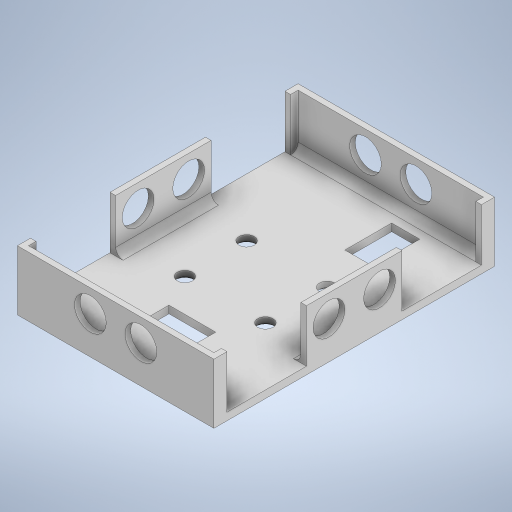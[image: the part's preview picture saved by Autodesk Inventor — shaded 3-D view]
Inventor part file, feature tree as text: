
AUTODESK INVENTOR PART (.ipt)
format: ipt  version: 2024.2 (Build 282272000, 272)  size: 484,352 bytes
history: native  units: mm
features: extrude x11, sketch x11, fillet x2, chamfer x1
ambient origin geometry x8: Origin, YZ Plane, XZ Plane, XY Plane, X Axis, Y Axis, Z Axis, Center Point
bodies: Solid1 (feature_tree)
feature tree (25):
  extrude  "Extrusion1"  Depth=48.0mm
  extrude  "Extrusion3"  Depth=4.7mm
  extrude  "Extrusion4"  Depth=4.7mm
  extrude  "remove legs"  Depth=43.0mm
  extrude  "Extrusion6"  Depth=7.5mm
  extrude  "Extrusion7"  Depth=7.5mm
  chamfer  "Chamfer1"  Distance=10.0mm
  sketch  "Sketch7"  dims[d12=7.500001mm]
  sketch  "Sketch8"  dims[d13=7.500001mm]
  sketch  "Sketch9"  dims[d14=10.0mm]
  extrude  "Extrusion10"  Depth=13.0mm TaperAngle=0.0deg
  extrude  "Extrusion11"  Depth=105.0mm
  extrude  "Extrusion12"  Depth=150.0mm
  extrude  "Extrusion13"  Depth=58.5mm
  fillet  "Fillet3"  Radius=31.0mm
  fillet  "Fillet4"  Radius=4.0mm
  extrude  "Extrusion14"  Depth=13.0mm
  sketch  "Sketch1"  dims[d0=58.0mm d1=48.0mm]
  sketch  "Sketch2"  dims[d2=4.7mm d3=4.7mm]
  sketch  "Sketch3"  dims[d4=4.7mm d5=4.7mm]
  sketch  "Sketch4"  dims[d6=33.0mm d7=43.0mm]
  sketch  "Sketch5"  dims[d8=7.5mm d9=7.5mm]
  sketch  "Sketch6"  dims[d10=7.5mm d11=7.5mm]
  sketch  "Sketch11"  dims[d15=10.0mm]
  sketch  "Sketch12"  dims[d16=10.0mm d17=10.0mm d18=12.0mm d19=0.0mm d20=105.0mm d21=150.0mm d22=58.5mm d23=31.0mm d26=4.0mm d27=0.0mm d28=20.0mm d45=28.0mm d46=0.0mm d48=20.0mm d49=3.0mm d50=3.0mm d51=3.0mm d52=3.0mm d53=20.0mm d55=20.0mm d56=20.0mm d57=3.0mm d59=100.0mm d60=15.0mm d61=25.0mm d62=0.0mm d63=8.2mm d64=8.2mm d65=8.2mm d66=8.2mm d67=4.0mm d68=0.0mm d69=20.0mm d72=25.0mm d73=15.0mm d74=15.0mm d75=25.0mm d76=22.0mm d77=2.5mm d78=9.0mm d79=17.5mm d80=10.0mm d81=0.0mm d82=1.0mm d83=2.0mm d84=45.0deg d88=3.0mm d89=51.0mm d91=3.0mm d92=51.0mm d95=17.0mm d96=65.0mm d102=3.0mm d103=17.0mm d104=65.0mm d105=17.0mm d106=17.0mm d107=17.0mm d108=27.0mm d109=20.0mm d113=17.0mm d114=17.0mm d115=20.0mm d116=49.5mm d117=28.0mm d118=0.0mm d119=61.5mm d120=0.0mm d121=0.0mm d122=0.0mm d123=0.0mm d124=20.0mm d125=39.0mm d126=27.0mm d127=13.0mm d128=0.0mm d129=0.0mm d130=4.0mm d131=4.0mm d132=13.0mm d133=0.0mm d134=0.0mm]
